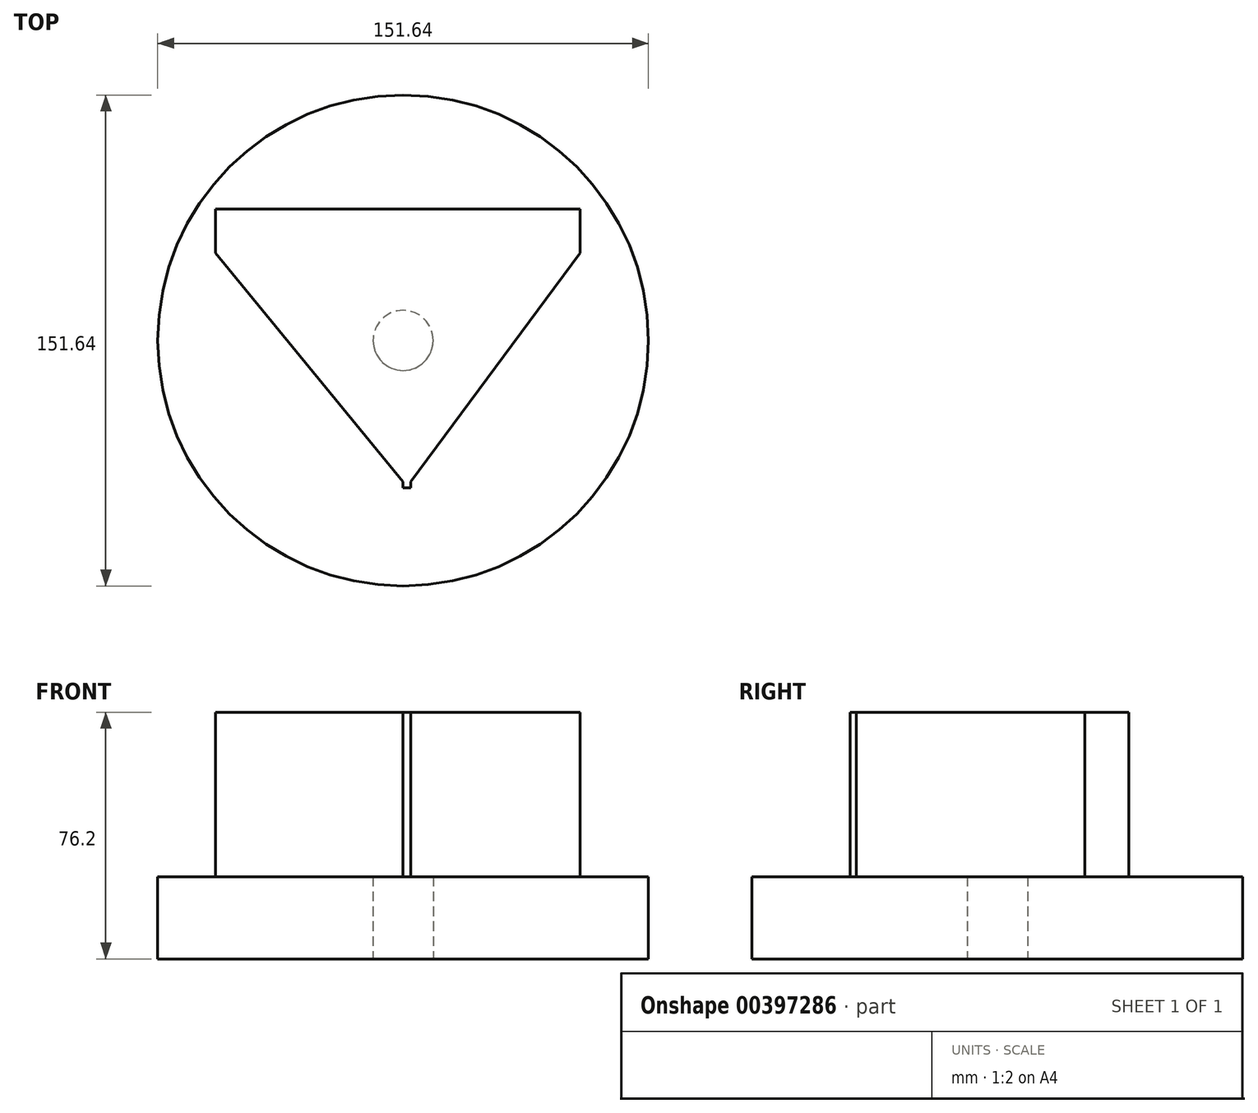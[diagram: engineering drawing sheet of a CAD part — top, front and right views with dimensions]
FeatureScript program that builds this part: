
annotation { "Feature Type Name" : "Feature", "Feature Type Description" : "" }
export const myFeature = defineFeature(function(context is Context, id is Id, definition is map)
    precondition{}
    {
        {
            var Q0;
            Q0=qCreatedBy(makeId("Top.planeOp"),FACE);
            var sketch = newSketch(context, id + "F0", { "sketchPlane" : qUnion([Q0])});
            skCircle(sketch, "E0", {"center": v(0, 0) * mm, "radius": 75.82 * mm});
            skCircle(sketch, "E1", {"center": v(0, 0) * mm, "radius": 9.3 * mm});
            skLineSegment(sketch, "E2", {"start": v(0, 0) * mm, "end": v(-75.82, 0) * mm});
            skLineSegment(sketch, "E3", {"start": v(0, 0) * mm, "end": v(75.82, 0) * mm});
            skSolve(sketch);
        }
        {
            var Q0;
            Q0 = qSketchRegion(id + "F0", true);
            extrude(context, id + "F1", {"entities" : qUnion([Q0]), "depth" : 25.4 * mm});
        }
        {
            var Q0;
            Q0=makeQuery(id+"F1.opExtrude","CAP_FACE",FACE,{"disambiguationData":[OSD([sQuery(id+"F0.wireOp",EDGE,"E0"),sQuery(id+"F0.wireOp",EDGE,"E1")])],"isStart":false});
            var sketch = newSketch(context, id + "F2", { "sketchPlane" : qUnion([Q0])});
            skLineSegment(sketch, "E4.bottom", {"start": v(-58, 27.03) * mm, "end": v(54.72, 27.03) * mm});
            skLineSegment(sketch, "E4.top", {"start": v(-58, 40.55) * mm, "end": v(54.72, 40.55) * mm});
            skLineSegment(sketch, "E4.left", {"start": v(-58, 27.03) * mm, "end": v(-58, 40.55) * mm});
            skLineSegment(sketch, "E4.right", {"start": v(54.72, 27.03) * mm, "end": v(54.72, 40.55) * mm});
            skLineSegment(sketch, "E5.bottom", {"start": v(0, -43.6) * mm, "end": v(2.4, -43.6) * mm});
            skLineSegment(sketch, "E5.top", {"start": v(0, -45.56) * mm, "end": v(2.4, -45.56) * mm});
            skLineSegment(sketch, "E5.left", {"start": v(0, -43.6) * mm, "end": v(0, -45.56) * mm});
            skLineSegment(sketch, "E5.right", {"start": v(2.4, -43.6) * mm, "end": v(2.4, -45.56) * mm});
            skSolve(sketch);
        }
        {
            var Q0;
            Q0 = qSketchRegion(id + "F2", true);
            extrude(context, id + "F3", {"entities" : qUnion([Q0]), "operationType" : NewBodyOperationType.ADD, "depth" : 25.4 * mm});
        }
        {
            var Q1;
            Q1=makeQuery(id+"F3.opExtrude","SWEPT_FACE",FACE,{"disambiguationData":[OSD([sQuery(id+"F2.wireOp",EDGE,"E4.bottom")])]});
            var Q2;
            Q2=makeQuery(id+"F3.opExtrude","SWEPT_FACE",FACE,{"disambiguationData":[OSD([sQuery(id+"F2.wireOp",EDGE,"E5.bottom")])]});
            loft(context, id + "F4", {"operationType" : NewBodyOperationType.ADD, "sheetProfilesArray" : [{ "sheetProfileEntities" : qUnion([Q1]) }, { "sheetProfileEntities" : qUnion([Q2]) }]});
        }
        {
            var Q0;
            {var subQ0=sQuery(id+"F2.wireOp",EDGE,"E5.bottom");var subQ1=sQuery(id+"F2.wireOp",EDGE,"E4.bottom");var subQ2=sQuery(id+"F2.wireOp",EDGE,"E5.right");var subQ3=sQuery(id+"F2.wireOp",EDGE,"E5.left");var subQ4=sQuery(id+"F2.wireOp",EDGE,"E4.right");var subQ5=sQuery(id+"F2.wireOp",EDGE,"E4.left");Q0=makeQuery(id+"F4.boolean.opBoolean","MERGE",FACE,{"derivedFrom":[makeQuery(id+"F3.opExtrude","CAP_FACE",FACE,{"disambiguationData":[OSD([subQ1,sQuery(id+"F2.wireOp",EDGE,"E4.top"),subQ5,subQ4])],"isStart":false}),makeQuery(id+"F3.opExtrude","CAP_FACE",FACE,{"disambiguationData":[OSD([subQ0,sQuery(id+"F2.wireOp",EDGE,"E5.top"),subQ3,subQ2])],"isStart":false}),makeQuery(id+"F4.opLoft","SWEPT_FACE",FACE,{"disambiguationData":[OSD([subQ1,subQ5,subQ4,subQ0,subQ3,subQ2]),TDD([makeQuery(id+"F3.opExtrude","CAP_VERTEX",VERTEX,{"disambiguationData":[OSD([subQ1,subQ5])],"isStart":false}),makeQuery(id+"F3.opExtrude","CAP_VERTEX",VERTEX,{"disambiguationData":[OSD([subQ1,subQ4])],"isStart":false}),makeQuery(id+"F3.opExtrude","CAP_VERTEX",VERTEX,{"disambiguationData":[OSD([subQ0,subQ3])],"isStart":false}),makeQuery(id+"F3.opExtrude","CAP_VERTEX",VERTEX,{"disambiguationData":[OSD([subQ0,subQ2])],"isStart":false}),makeQuery(id+"F3.opExtrude","CAP_EDGE",EDGE,{"disambiguationData":[OSD([subQ1])],"isStart":false}),makeQuery(id+"F3.opExtrude","CAP_EDGE",EDGE,{"disambiguationData":[OSD([subQ0])],"isStart":false})])]})]});}
            extrude(context, id + "F5", {"entities" : qUnion([Q0]), "operationType" : NewBodyOperationType.ADD, "depth" : 25.4 * mm});
        }
    });
